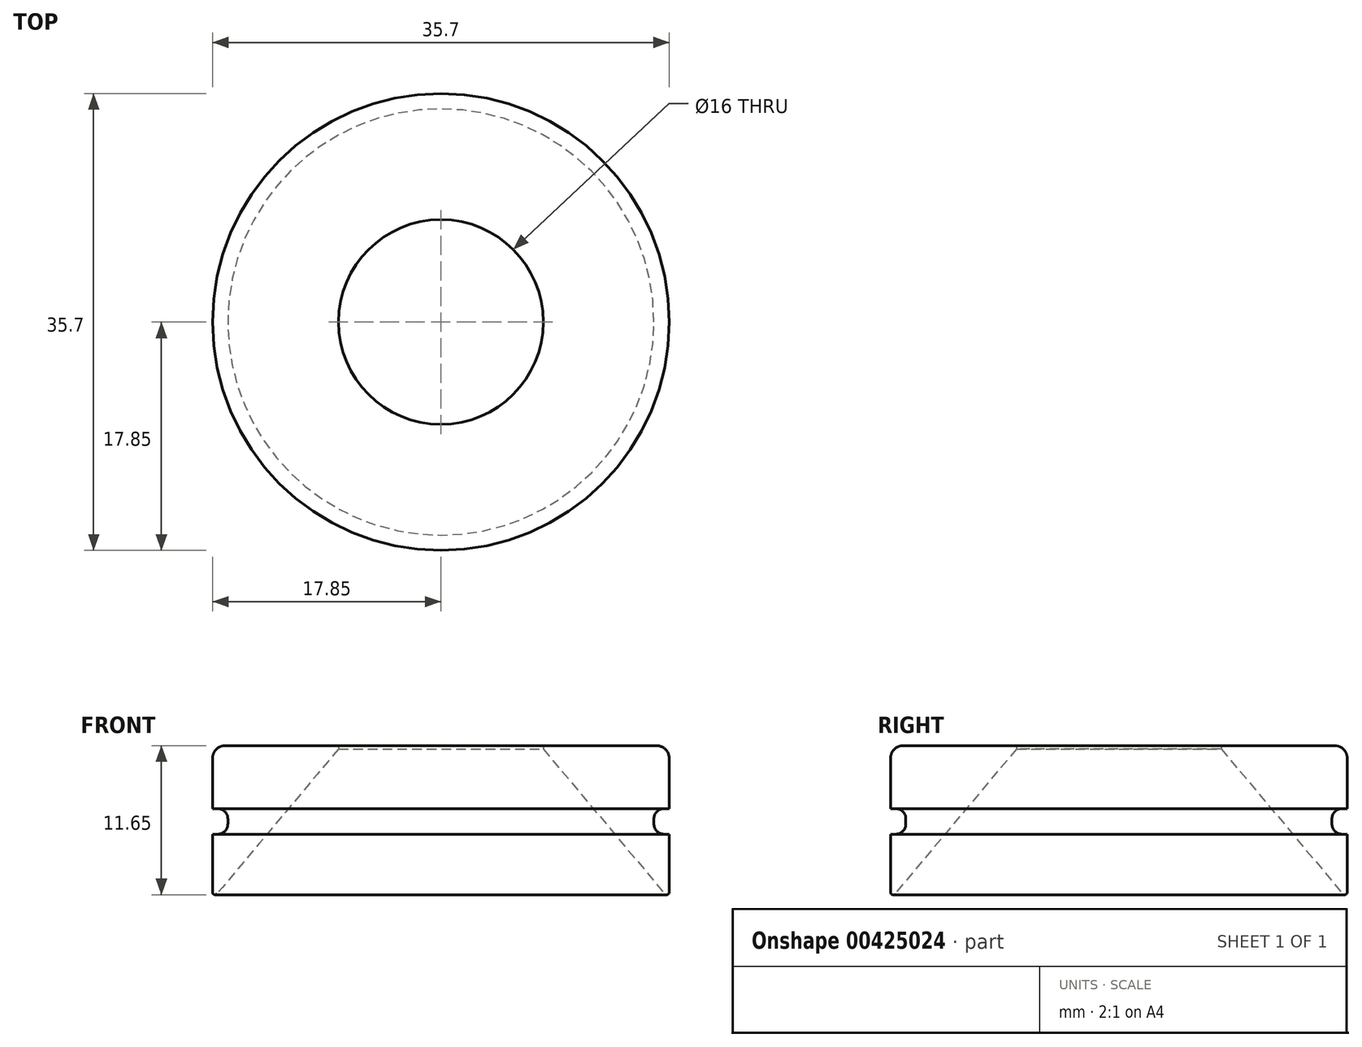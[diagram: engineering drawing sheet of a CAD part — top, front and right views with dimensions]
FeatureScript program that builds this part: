
annotation { "Feature Type Name" : "Feature", "Feature Type Description" : "" }
export const myFeature = defineFeature(function(context is Context, id is Id, definition is map)
    precondition{}
    {
        {
            var Q0;
            Q0=qCreatedBy(makeId("Front.planeOp"),FACE);
            var sketch = newSketch(context, id + "F0", { "sketchPlane" : qUnion([Q0])});
            skLineSegment(sketch, "E0", {"start": v(17.85, 0) * mm, "end": v(17.85, 12) * mm});
            skLineSegment(sketch, "E1", {"start": v(17.85, 0) * mm, "end": v(7.78, 12) * mm});
            skLineSegment(sketch, "E2", {"start": v(17.85, 12) * mm, "end": v(7.78, 12) * mm});
            skLineSegment(sketch, "E3", {"start": v(0, 0) * mm, "end": v(0, 9.48) * mm, "construction": true});
            skLineSegment(sketch, "E4.bottom", {"start": v(17.85, 7.08) * mm, "end": v(16.65, 7.08) * mm});
            skLineSegment(sketch, "E4.top", {"start": v(17.85, 5.08) * mm, "end": v(16.65, 5.08) * mm});
            skLineSegment(sketch, "E4.left", {"start": v(17.85, 7.08) * mm, "end": v(17.85, 5.08) * mm});
            skLineSegment(sketch, "E4.right", {"start": v(16.65, 7.08) * mm, "end": v(16.65, 5.08) * mm});
            skLineSegment(sketch, "E5", {"start": v(8, 12) * mm, "end": v(8, 11.74) * mm});
            skSolve(sketch);
        }
        {
            var Q0;
            {var subQ7=sQuery(id+"F0.wireOp",EDGE,"E4.bottom");Q0=makeQuery(id+"F0.imprint","IMPRINT",FACE,{"disambiguationData":[TD([[makeQuery(id+"F0.imprint","IMPRINT",EDGE,{"derivedFrom":subQ7}),-1.0]])]});}
            var Q1;
            Q1=sQuery(id+"F0.wireOp",EDGE,"E3");
            revolve(context, id + "F1", {"entities" : qUnion([Q0]), "axis" : qUnion([Q1]), "revolveType" : RevolveType.FULL});
        }
        {
            var Q0;
            Q0=makeQuery(id+"F1.opRevolve","SWEPT_EDGE",EDGE,{"disambiguationData":[OSD([sQuery(id+"F0.wireOp",EDGE,"E0"),sQuery(id+"F0.wireOp",EDGE,"E2")])]});
            fillet(context, id + "F2", {"entities" : qUnion([Q0]), "radius" : 1 * mm, "tangentPropagation" : true, "allowEdgeOverflow" : false});
        }
        {
            var Q0;
            Q0=makeQuery(id+"F1.opRevolve","SWEPT_EDGE",EDGE,{"disambiguationData":[OSD([sQuery(id+"F0.wireOp",EDGE,"E4.bottom"),sQuery(id+"F0.wireOp",EDGE,"E4.right")])]});
            var Q1;
            Q1=makeQuery(id+"F1.opRevolve","SWEPT_EDGE",EDGE,{"disambiguationData":[OSD([sQuery(id+"F0.wireOp",EDGE,"E4.top"),sQuery(id+"F0.wireOp",EDGE,"E4.right")])]});
            fillet(context, id + "F3", {"entities" : qUnion([Q0, Q1]), "radius" : .8 * mm, "tangentPropagation" : true, "allowEdgeOverflow" : false});
        }
        {
            var Q0;
            Q0=makeQuery(id+"F1.opRevolve","SWEPT_EDGE",EDGE,{"disambiguationData":[OSD([sQuery(id+"F0.wireOp",EDGE,"E0"),sQuery(id+"F0.wireOp",EDGE,"E1")])]});
            fillet(context, id + "F4", {"entities" : qUnion([Q0]), "radius" : .2 * mm, "tangentPropagation" : true, "allowEdgeOverflow" : false});
        }
    });
